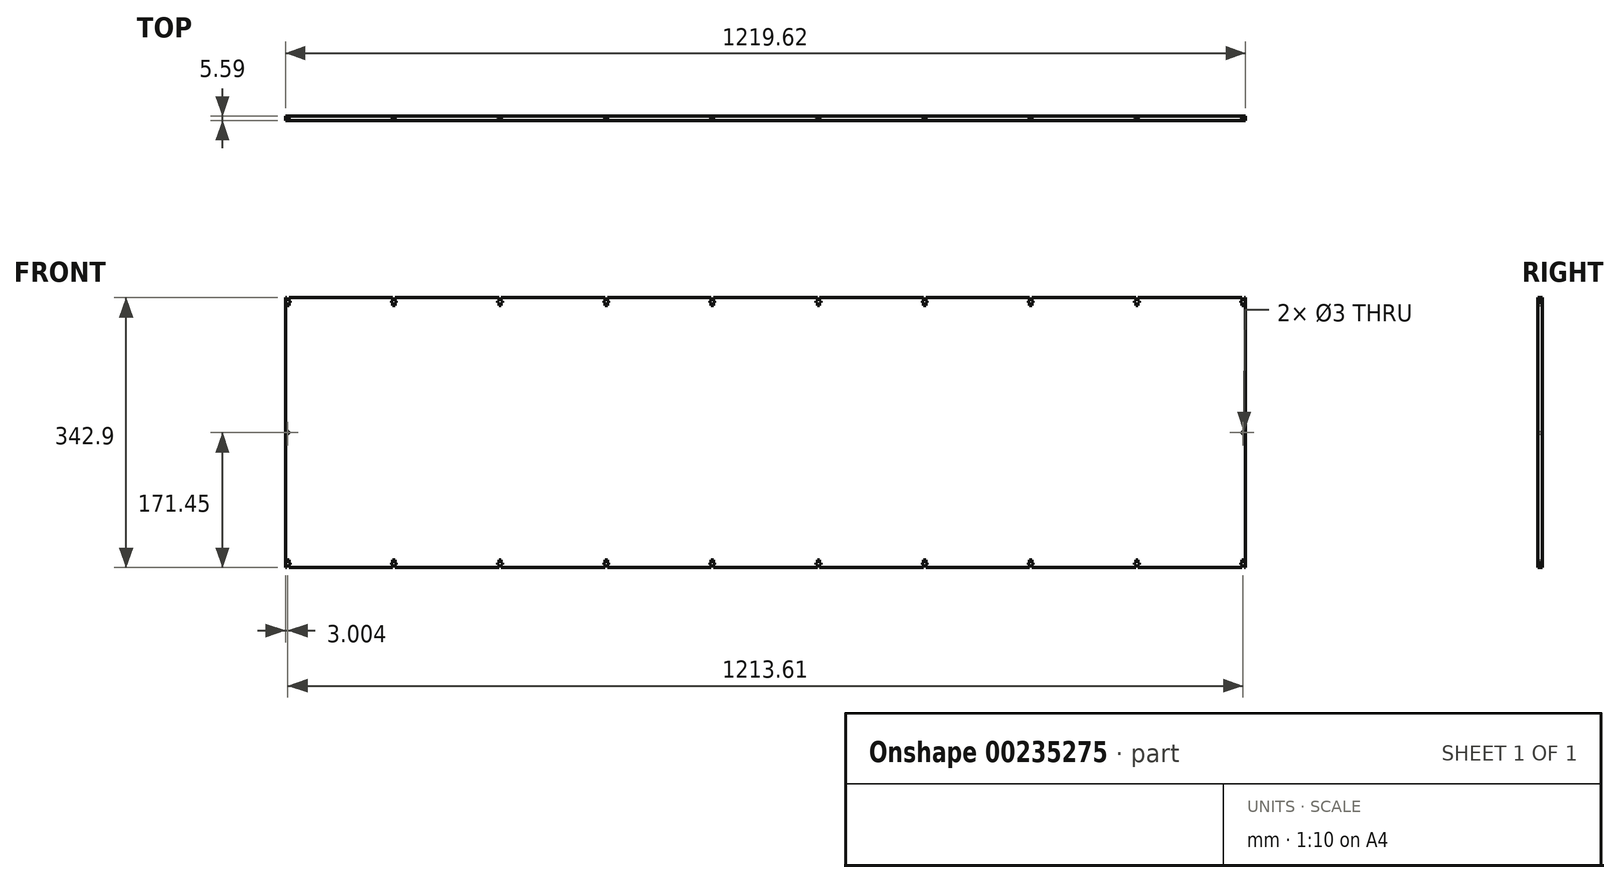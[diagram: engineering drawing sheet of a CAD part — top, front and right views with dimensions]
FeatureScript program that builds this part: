
annotation { "Feature Type Name" : "Feature", "Feature Type Description" : "" }
export const myFeature = defineFeature(function(context is Context, id is Id, definition is map)
    precondition{}
    {
        {
            var Q0;
            Q0=qCreatedBy(makeId("Front.planeOp"),FACE);
            var sketch = newSketch(context, id + "F0", { "sketchPlane" : qUnion([Q0])});
            skLineSegment(sketch, "E0.bottom", {"start": v(-609.6, 171.45) * mm, "end": v(-608.3, 171.45) * mm});
            skLineSegment(sketch, "E0.top", {"start": v(-609.6, -171.45) * mm, "end": v(-608.3, -171.45) * mm});
            skLineSegment(sketch, "E0.left", {"start": v(-609.6, 171.45) * mm, "end": v(-609.6, -171.45) * mm});
            skLineSegment(sketch, "E0.right", {"start": v(609.6, 171.45) * mm, "end": v(609.6, -171.45) * mm});
            skPoint(sketch, "E0.middle", {"position": v(0, 0) * mm});
            skLineSegment(sketch, "E1", {"start": v(-609.6, 171.45) * mm, "end": v(-608.3, 171.45) * mm, "construction": true});
            skLineSegment(sketch, "E2", {"start": v(-606.8, 171.45) * mm, "end": v(-606.8, 139.65) * mm, "construction": true});
            skLineSegment(sketch, "E3", {"start": v(-608.3, 171.45) * mm, "end": v(-608.3, 167.45) * mm});
            skLineSegment(sketch, "E4", {"start": v(-608.3, 167.45) * mm, "end": v(-609.8, 167.45) * mm});
            skLineSegment(sketch, "E5", {"start": v(-609.8, 167.45) * mm, "end": v(-609.8, 165.45) * mm});
            skLineSegment(sketch, "E6", {"start": v(-609.8, 165.45) * mm, "end": v(-608.3, 165.45) * mm});
            skLineSegment(sketch, "E7", {"start": v(-608.3, 165.45) * mm, "end": v(-608.3, 161.45) * mm});
            skLineSegment(sketch, "E8", {"start": v(-608.3, 161.45) * mm, "end": v(-605.3, 161.45) * mm});
            skLineSegment(sketch, "E9", {"start": v(-605.3, 161.45) * mm, "end": v(-605.3, 165.45) * mm});
            skLineSegment(sketch, "E10", {"start": v(-605.3, 165.45) * mm, "end": v(-603.8, 165.45) * mm});
            skLineSegment(sketch, "E11", {"start": v(-603.8, 165.45) * mm, "end": v(-603.8, 167.45) * mm});
            skLineSegment(sketch, "E12", {"start": v(-603.8, 167.45) * mm, "end": v(-605.3, 167.45) * mm});
            skLineSegment(sketch, "E13", {"start": v(-605.3, 167.45) * mm, "end": v(-605.3, 171.45) * mm});
            skLineSegment(sketch, "E14.trimOffspring", {"start": v(-605.3, 171.45) * mm, "end": v(-473.46, 171.45) * mm});
            skLineSegment(sketch, "E15.1.0.0", {"start": v(-470.46, 167.45) * mm, "end": v(-470.46, 171.45) * mm});
            skLineSegment(sketch, "E15.1.0.1", {"start": v(-470.46, 161.45) * mm, "end": v(-470.46, 165.45) * mm});
            skLineSegment(sketch, "E15.1.0.2", {"start": v(-470.46, 165.45) * mm, "end": v(-468.96, 165.45) * mm});
            skLineSegment(sketch, "E15.1.0.3", {"start": v(-468.96, 165.45) * mm, "end": v(-468.96, 167.45) * mm});
            skLineSegment(sketch, "E15.1.0.4", {"start": v(-471.96, 171.45) * mm, "end": v(-471.96, 139.65) * mm, "construction": true});
            skLineSegment(sketch, "E15.1.0.5", {"start": v(-473.46, 171.45) * mm, "end": v(-473.46, 167.45) * mm});
            skLineSegment(sketch, "E15.1.0.6", {"start": v(-473.46, 167.45) * mm, "end": v(-474.96, 167.45) * mm});
            skLineSegment(sketch, "E15.1.0.7", {"start": v(-474.96, 167.45) * mm, "end": v(-474.96, 165.45) * mm});
            skLineSegment(sketch, "E15.1.0.8", {"start": v(-474.96, 165.45) * mm, "end": v(-473.46, 165.45) * mm});
            skLineSegment(sketch, "E15.1.0.9", {"start": v(-473.46, 165.45) * mm, "end": v(-473.46, 161.45) * mm});
            skLineSegment(sketch, "E15.1.0.10", {"start": v(-473.46, 161.45) * mm, "end": v(-470.46, 161.45) * mm});
            skLineSegment(sketch, "E15.1.0.11", {"start": v(-468.96, 167.45) * mm, "end": v(-470.46, 167.45) * mm});
            skLineSegment(sketch, "E15.2.0.0", {"start": v(-335.61, 167.45) * mm, "end": v(-335.61, 171.45) * mm});
            skLineSegment(sketch, "E15.2.0.1", {"start": v(-335.61, 161.45) * mm, "end": v(-335.61, 165.45) * mm});
            skLineSegment(sketch, "E15.2.0.2", {"start": v(-335.61, 165.45) * mm, "end": v(-334.11, 165.45) * mm});
            skLineSegment(sketch, "E15.2.0.3", {"start": v(-334.11, 165.45) * mm, "end": v(-334.11, 167.45) * mm});
            skLineSegment(sketch, "E15.2.0.4", {"start": v(-337.11, 171.45) * mm, "end": v(-337.11, 139.65) * mm, "construction": true});
            skLineSegment(sketch, "E15.2.0.5", {"start": v(-338.61, 171.45) * mm, "end": v(-338.61, 167.45) * mm});
            skLineSegment(sketch, "E15.2.0.6", {"start": v(-338.61, 167.45) * mm, "end": v(-340.11, 167.45) * mm});
            skLineSegment(sketch, "E15.2.0.7", {"start": v(-340.11, 167.45) * mm, "end": v(-340.11, 165.45) * mm});
            skLineSegment(sketch, "E15.2.0.8", {"start": v(-340.11, 165.45) * mm, "end": v(-338.61, 165.45) * mm});
            skLineSegment(sketch, "E15.2.0.9", {"start": v(-338.61, 165.45) * mm, "end": v(-338.61, 161.45) * mm});
            skLineSegment(sketch, "E15.2.0.10", {"start": v(-338.61, 161.45) * mm, "end": v(-335.61, 161.45) * mm});
            skLineSegment(sketch, "E15.2.0.11", {"start": v(-334.11, 167.45) * mm, "end": v(-335.61, 167.45) * mm});
            skLineSegment(sketch, "E15.3.0.0", {"start": v(-200.77, 167.45) * mm, "end": v(-200.77, 171.45) * mm});
            skLineSegment(sketch, "E15.3.0.1", {"start": v(-200.77, 161.45) * mm, "end": v(-200.77, 165.45) * mm});
            skLineSegment(sketch, "E15.3.0.2", {"start": v(-200.77, 165.45) * mm, "end": v(-199.27, 165.45) * mm});
            skLineSegment(sketch, "E15.3.0.3", {"start": v(-199.27, 165.45) * mm, "end": v(-199.27, 167.45) * mm});
            skLineSegment(sketch, "E15.3.0.4", {"start": v(-202.27, 171.45) * mm, "end": v(-202.27, 139.65) * mm, "construction": true});
            skLineSegment(sketch, "E15.3.0.5", {"start": v(-203.77, 171.45) * mm, "end": v(-203.77, 167.45) * mm});
            skLineSegment(sketch, "E15.3.0.6", {"start": v(-203.77, 167.45) * mm, "end": v(-205.27, 167.45) * mm});
            skLineSegment(sketch, "E15.3.0.7", {"start": v(-205.27, 167.45) * mm, "end": v(-205.27, 165.45) * mm});
            skLineSegment(sketch, "E15.3.0.8", {"start": v(-205.27, 165.45) * mm, "end": v(-203.77, 165.45) * mm});
            skLineSegment(sketch, "E15.3.0.9", {"start": v(-203.77, 165.45) * mm, "end": v(-203.77, 161.45) * mm});
            skLineSegment(sketch, "E15.3.0.10", {"start": v(-203.77, 161.45) * mm, "end": v(-200.77, 161.45) * mm});
            skLineSegment(sketch, "E15.3.0.11", {"start": v(-199.27, 167.45) * mm, "end": v(-200.77, 167.45) * mm});
            skLineSegment(sketch, "E15.4.0.0", {"start": v(-65.92, 167.45) * mm, "end": v(-65.92, 171.45) * mm});
            skLineSegment(sketch, "E15.4.0.1", {"start": v(-65.92, 161.45) * mm, "end": v(-65.92, 165.45) * mm});
            skLineSegment(sketch, "E15.4.0.2", {"start": v(-65.92, 165.45) * mm, "end": v(-64.42, 165.45) * mm});
            skLineSegment(sketch, "E15.4.0.3", {"start": v(-64.42, 165.45) * mm, "end": v(-64.42, 167.45) * mm});
            skLineSegment(sketch, "E15.4.0.4", {"start": v(-67.42, 171.45) * mm, "end": v(-67.42, 139.65) * mm, "construction": true});
            skLineSegment(sketch, "E15.4.0.5", {"start": v(-68.92, 171.45) * mm, "end": v(-68.92, 167.45) * mm});
            skLineSegment(sketch, "E15.4.0.6", {"start": v(-68.92, 167.45) * mm, "end": v(-70.42, 167.45) * mm});
            skLineSegment(sketch, "E15.4.0.7", {"start": v(-70.42, 167.45) * mm, "end": v(-70.42, 165.45) * mm});
            skLineSegment(sketch, "E15.4.0.8", {"start": v(-70.42, 165.45) * mm, "end": v(-68.92, 165.45) * mm});
            skLineSegment(sketch, "E15.4.0.9", {"start": v(-68.92, 165.45) * mm, "end": v(-68.92, 161.45) * mm});
            skLineSegment(sketch, "E15.4.0.10", {"start": v(-68.92, 161.45) * mm, "end": v(-65.92, 161.45) * mm});
            skLineSegment(sketch, "E15.4.0.11", {"start": v(-64.42, 167.45) * mm, "end": v(-65.92, 167.45) * mm});
            skLineSegment(sketch, "E15.5.0.0", {"start": v(68.92, 167.45) * mm, "end": v(68.92, 171.45) * mm});
            skLineSegment(sketch, "E15.5.0.1", {"start": v(68.92, 161.45) * mm, "end": v(68.92, 165.45) * mm});
            skLineSegment(sketch, "E15.5.0.2", {"start": v(68.92, 165.45) * mm, "end": v(70.42, 165.45) * mm});
            skLineSegment(sketch, "E15.5.0.3", {"start": v(70.42, 165.45) * mm, "end": v(70.42, 167.45) * mm});
            skLineSegment(sketch, "E15.5.0.4", {"start": v(67.42, 171.45) * mm, "end": v(67.42, 139.65) * mm, "construction": true});
            skLineSegment(sketch, "E15.5.0.5", {"start": v(65.92, 171.45) * mm, "end": v(65.92, 167.45) * mm});
            skLineSegment(sketch, "E15.5.0.6", {"start": v(65.92, 167.45) * mm, "end": v(64.42, 167.45) * mm});
            skLineSegment(sketch, "E15.5.0.7", {"start": v(64.42, 167.45) * mm, "end": v(64.42, 165.45) * mm});
            skLineSegment(sketch, "E15.5.0.8", {"start": v(64.42, 165.45) * mm, "end": v(65.92, 165.45) * mm});
            skLineSegment(sketch, "E15.5.0.9", {"start": v(65.92, 165.45) * mm, "end": v(65.92, 161.45) * mm});
            skLineSegment(sketch, "E15.5.0.10", {"start": v(65.92, 161.45) * mm, "end": v(68.92, 161.45) * mm});
            skLineSegment(sketch, "E15.5.0.11", {"start": v(70.42, 167.45) * mm, "end": v(68.92, 167.45) * mm});
            skLineSegment(sketch, "E15.6.0.0", {"start": v(203.77, 167.45) * mm, "end": v(203.77, 171.45) * mm});
            skLineSegment(sketch, "E15.6.0.1", {"start": v(203.77, 161.45) * mm, "end": v(203.77, 165.45) * mm});
            skLineSegment(sketch, "E15.6.0.2", {"start": v(203.77, 165.45) * mm, "end": v(205.27, 165.45) * mm});
            skLineSegment(sketch, "E15.6.0.3", {"start": v(205.27, 165.45) * mm, "end": v(205.27, 167.45) * mm});
            skLineSegment(sketch, "E15.6.0.4", {"start": v(202.27, 171.45) * mm, "end": v(202.27, 139.65) * mm, "construction": true});
            skLineSegment(sketch, "E15.6.0.5", {"start": v(200.77, 171.45) * mm, "end": v(200.77, 167.45) * mm});
            skLineSegment(sketch, "E15.6.0.6", {"start": v(200.77, 167.45) * mm, "end": v(199.27, 167.45) * mm});
            skLineSegment(sketch, "E15.6.0.7", {"start": v(199.27, 167.45) * mm, "end": v(199.27, 165.45) * mm});
            skLineSegment(sketch, "E15.6.0.8", {"start": v(199.27, 165.45) * mm, "end": v(200.77, 165.45) * mm});
            skLineSegment(sketch, "E15.6.0.9", {"start": v(200.77, 165.45) * mm, "end": v(200.77, 161.45) * mm});
            skLineSegment(sketch, "E15.6.0.10", {"start": v(200.77, 161.45) * mm, "end": v(203.77, 161.45) * mm});
            skLineSegment(sketch, "E15.6.0.11", {"start": v(205.27, 167.45) * mm, "end": v(203.77, 167.45) * mm});
            skLineSegment(sketch, "E15.7.0.0", {"start": v(338.62, 167.45) * mm, "end": v(338.62, 171.45) * mm});
            skLineSegment(sketch, "E15.7.0.1", {"start": v(338.62, 161.45) * mm, "end": v(338.62, 165.45) * mm});
            skLineSegment(sketch, "E15.7.0.2", {"start": v(338.62, 165.45) * mm, "end": v(340.12, 165.45) * mm});
            skLineSegment(sketch, "E15.7.0.3", {"start": v(340.12, 165.45) * mm, "end": v(340.12, 167.45) * mm});
            skLineSegment(sketch, "E15.7.0.4", {"start": v(337.12, 171.45) * mm, "end": v(337.12, 139.65) * mm, "construction": true});
            skLineSegment(sketch, "E15.7.0.5", {"start": v(335.62, 171.45) * mm, "end": v(335.62, 167.45) * mm});
            skLineSegment(sketch, "E15.7.0.6", {"start": v(335.62, 167.45) * mm, "end": v(334.12, 167.45) * mm});
            skLineSegment(sketch, "E15.7.0.7", {"start": v(334.12, 167.45) * mm, "end": v(334.12, 165.45) * mm});
            skLineSegment(sketch, "E15.7.0.8", {"start": v(334.12, 165.45) * mm, "end": v(335.62, 165.45) * mm});
            skLineSegment(sketch, "E15.7.0.9", {"start": v(335.62, 165.45) * mm, "end": v(335.62, 161.45) * mm});
            skLineSegment(sketch, "E15.7.0.10", {"start": v(335.62, 161.45) * mm, "end": v(338.62, 161.45) * mm});
            skLineSegment(sketch, "E15.7.0.11", {"start": v(340.12, 167.45) * mm, "end": v(338.62, 167.45) * mm});
            skLineSegment(sketch, "E15.8.0.0", {"start": v(473.46, 167.45) * mm, "end": v(473.46, 171.45) * mm});
            skLineSegment(sketch, "E15.8.0.1", {"start": v(473.46, 161.45) * mm, "end": v(473.46, 165.45) * mm});
            skLineSegment(sketch, "E15.8.0.2", {"start": v(473.46, 165.45) * mm, "end": v(474.96, 165.45) * mm});
            skLineSegment(sketch, "E15.8.0.3", {"start": v(474.96, 165.45) * mm, "end": v(474.96, 167.45) * mm});
            skLineSegment(sketch, "E15.8.0.4", {"start": v(471.96, 171.45) * mm, "end": v(471.96, 139.65) * mm, "construction": true});
            skLineSegment(sketch, "E15.8.0.5", {"start": v(470.46, 171.45) * mm, "end": v(470.46, 167.45) * mm});
            skLineSegment(sketch, "E15.8.0.6", {"start": v(470.46, 167.45) * mm, "end": v(468.96, 167.45) * mm});
            skLineSegment(sketch, "E15.8.0.7", {"start": v(468.96, 167.45) * mm, "end": v(468.96, 165.45) * mm});
            skLineSegment(sketch, "E15.8.0.8", {"start": v(468.96, 165.45) * mm, "end": v(470.46, 165.45) * mm});
            skLineSegment(sketch, "E15.8.0.9", {"start": v(470.46, 165.45) * mm, "end": v(470.46, 161.45) * mm});
            skLineSegment(sketch, "E15.8.0.10", {"start": v(470.46, 161.45) * mm, "end": v(473.46, 161.45) * mm});
            skLineSegment(sketch, "E15.8.0.11", {"start": v(474.96, 167.45) * mm, "end": v(473.46, 167.45) * mm});
            skLineSegment(sketch, "E15.9.0.0", {"start": v(608.3, 167.45) * mm, "end": v(608.3, 171.45) * mm});
            skLineSegment(sketch, "E15.9.0.1", {"start": v(608.3, 161.45) * mm, "end": v(608.3, 165.45) * mm});
            skLineSegment(sketch, "E15.9.0.2", {"start": v(608.3, 165.45) * mm, "end": v(609.8, 165.45) * mm});
            skLineSegment(sketch, "E15.9.0.3", {"start": v(609.8, 165.45) * mm, "end": v(609.8, 167.45) * mm});
            skLineSegment(sketch, "E15.9.0.4", {"start": v(606.8, 171.45) * mm, "end": v(606.8, 139.65) * mm, "construction": true});
            skLineSegment(sketch, "E15.9.0.5", {"start": v(605.3, 171.45) * mm, "end": v(605.3, 167.45) * mm});
            skLineSegment(sketch, "E15.9.0.6", {"start": v(605.3, 167.45) * mm, "end": v(603.8, 167.45) * mm});
            skLineSegment(sketch, "E15.9.0.7", {"start": v(603.8, 167.45) * mm, "end": v(603.8, 165.45) * mm});
            skLineSegment(sketch, "E15.9.0.8", {"start": v(603.8, 165.45) * mm, "end": v(605.3, 165.45) * mm});
            skLineSegment(sketch, "E15.9.0.9", {"start": v(605.3, 165.45) * mm, "end": v(605.3, 161.45) * mm});
            skLineSegment(sketch, "E15.9.0.10", {"start": v(605.3, 161.45) * mm, "end": v(608.3, 161.45) * mm});
            skLineSegment(sketch, "E15.9.0.11", {"start": v(609.8, 167.45) * mm, "end": v(608.3, 167.45) * mm});
            skLineSegment(sketch, "E15.direction1", {"start": v(-606.8, 139.65) * mm, "end": v(-471.96, 139.65) * mm, "construction": true});
            skLineSegment(sketch, "E16.trimOffspring", {"start": v(608.3, 171.45) * mm, "end": v(609.6, 171.45) * mm});
            skLineSegment(sketch, "E17.trimOffspring", {"start": v(473.46, 171.45) * mm, "end": v(605.3, 171.45) * mm});
            skLineSegment(sketch, "E18.trimOffspring", {"start": v(338.62, 171.45) * mm, "end": v(470.46, 171.45) * mm});
            skLineSegment(sketch, "E19.trimOffspring", {"start": v(203.77, 171.45) * mm, "end": v(335.62, 171.45) * mm});
            skLineSegment(sketch, "E20.trimOffspring", {"start": v(68.92, 171.45) * mm, "end": v(200.77, 171.45) * mm});
            skLineSegment(sketch, "E21.trimOffspring", {"start": v(-65.92, 171.45) * mm, "end": v(65.92, 171.45) * mm});
            skLineSegment(sketch, "E22.trimOffspring", {"start": v(-200.77, 171.45) * mm, "end": v(-68.92, 171.45) * mm});
            skLineSegment(sketch, "E23.trimOffspring", {"start": v(-335.61, 171.45) * mm, "end": v(-203.77, 171.45) * mm});
            skLineSegment(sketch, "E24.trimOffspring", {"start": v(-470.46, 171.45) * mm, "end": v(-338.61, 171.45) * mm});
            skLineSegment(sketch, "E25", {"start": v(0, 0) * mm, "end": v(-483.43, 0) * mm, "construction": true});
            skLineSegment(sketch, "E26.MirrorCS", {"start": v(-603.8, -167.45) * mm, "end": v(-605.3, -167.45) * mm});
            skLineSegment(sketch, "E27.MirrorCS", {"start": v(-605.3, -161.45) * mm, "end": v(-605.3, -165.45) * mm});
            skLineSegment(sketch, "E28.MirrorCS", {"start": v(-605.3, -165.45) * mm, "end": v(-603.8, -165.45) * mm});
            skLineSegment(sketch, "E29.MirrorCS", {"start": v(-603.8, -165.45) * mm, "end": v(-603.8, -167.45) * mm});
            skLineSegment(sketch, "E30.MirrorCS", {"start": v(-606.8, -171.45) * mm, "end": v(-606.8, -139.65) * mm, "construction": true});
            skLineSegment(sketch, "E31.MirrorCS", {"start": v(-608.3, -171.45) * mm, "end": v(-608.3, -167.45) * mm});
            skLineSegment(sketch, "E32.MirrorCS", {"start": v(-608.3, -167.45) * mm, "end": v(-609.8, -167.45) * mm});
            skLineSegment(sketch, "E33.MirrorCS", {"start": v(-605.3, -167.45) * mm, "end": v(-605.3, -171.45) * mm});
            skLineSegment(sketch, "E34.MirrorCS", {"start": v(-608.3, -165.45) * mm, "end": v(-608.3, -161.45) * mm});
            skLineSegment(sketch, "E35.MirrorCS", {"start": v(-608.3, -161.45) * mm, "end": v(-605.3, -161.45) * mm});
            skLineSegment(sketch, "E36.MirrorCS", {"start": v(-609.8, -165.45) * mm, "end": v(-608.3, -165.45) * mm});
            skLineSegment(sketch, "E37.MirrorCS", {"start": v(-609.8, -167.45) * mm, "end": v(-609.8, -165.45) * mm});
            skLineSegment(sketch, "E38.MirrorCS", {"start": v(-470.46, -165.45) * mm, "end": v(-468.96, -165.45) * mm});
            skLineSegment(sketch, "E39.MirrorCS", {"start": v(-468.96, -165.45) * mm, "end": v(-468.96, -167.45) * mm});
            skLineSegment(sketch, "E40.MirrorCS", {"start": v(-473.46, -167.45) * mm, "end": v(-474.96, -167.45) * mm});
            skLineSegment(sketch, "E41.MirrorCS", {"start": v(-474.96, -167.45) * mm, "end": v(-474.96, -165.45) * mm});
            skLineSegment(sketch, "E42.MirrorCS", {"start": v(-474.96, -165.45) * mm, "end": v(-473.46, -165.45) * mm});
            skLineSegment(sketch, "E43.MirrorCS", {"start": v(-468.96, -167.45) * mm, "end": v(-470.46, -167.45) * mm});
            skLineSegment(sketch, "E44.MirrorCS", {"start": v(-470.46, -167.45) * mm, "end": v(-470.46, -171.45) * mm});
            skLineSegment(sketch, "E45.MirrorCS", {"start": v(-470.46, -161.45) * mm, "end": v(-470.46, -165.45) * mm});
            skLineSegment(sketch, "E46.MirrorCS", {"start": v(-471.96, -171.45) * mm, "end": v(-471.96, -139.65) * mm, "construction": true});
            skLineSegment(sketch, "E47.MirrorCS", {"start": v(-473.46, -171.45) * mm, "end": v(-473.46, -167.45) * mm});
            skLineSegment(sketch, "E48.MirrorCS", {"start": v(-473.46, -161.45) * mm, "end": v(-470.46, -161.45) * mm});
            skLineSegment(sketch, "E49.MirrorCS", {"start": v(-473.46, -165.45) * mm, "end": v(-473.46, -161.45) * mm});
            skLineSegment(sketch, "E50.MirrorCS", {"start": v(-334.11, -165.45) * mm, "end": v(-334.11, -167.45) * mm});
            skLineSegment(sketch, "E51.MirrorCS", {"start": v(-335.61, -165.45) * mm, "end": v(-334.11, -165.45) * mm});
            skLineSegment(sketch, "E52.MirrorCS", {"start": v(-334.11, -167.45) * mm, "end": v(-335.61, -167.45) * mm});
            skLineSegment(sketch, "E53.MirrorCS", {"start": v(-340.11, -165.45) * mm, "end": v(-338.61, -165.45) * mm});
            skLineSegment(sketch, "E54.MirrorCS", {"start": v(-340.11, -167.45) * mm, "end": v(-340.11, -165.45) * mm});
            skLineSegment(sketch, "E55.MirrorCS", {"start": v(-338.61, -167.45) * mm, "end": v(-340.11, -167.45) * mm});
            skLineSegment(sketch, "E56.MirrorCS", {"start": v(-335.61, -161.45) * mm, "end": v(-335.61, -165.45) * mm});
            skLineSegment(sketch, "E57.MirrorCS", {"start": v(-337.11, -171.45) * mm, "end": v(-337.11, -139.65) * mm, "construction": true});
            skLineSegment(sketch, "E58.MirrorCS", {"start": v(-335.61, -167.45) * mm, "end": v(-335.61, -171.45) * mm});
            skLineSegment(sketch, "E59.MirrorCS", {"start": v(-338.61, -161.45) * mm, "end": v(-335.61, -161.45) * mm});
            skLineSegment(sketch, "E60.MirrorCS", {"start": v(-338.61, -165.45) * mm, "end": v(-338.61, -161.45) * mm});
            skLineSegment(sketch, "E61.MirrorCS", {"start": v(-338.61, -171.45) * mm, "end": v(-338.61, -167.45) * mm});
            skLineSegment(sketch, "E62.MirrorCS", {"start": v(-205.27, -167.45) * mm, "end": v(-205.27, -165.45) * mm});
            skLineSegment(sketch, "E63.MirrorCS", {"start": v(-203.77, -167.45) * mm, "end": v(-205.27, -167.45) * mm});
            skLineSegment(sketch, "E64.MirrorCS", {"start": v(-205.27, -165.45) * mm, "end": v(-203.77, -165.45) * mm});
            skLineSegment(sketch, "E65.MirrorCS", {"start": v(-199.27, -167.45) * mm, "end": v(-200.77, -167.45) * mm});
            skLineSegment(sketch, "E66.MirrorCS", {"start": v(-200.77, -165.45) * mm, "end": v(-199.27, -165.45) * mm});
            skLineSegment(sketch, "E67.MirrorCS", {"start": v(-199.27, -165.45) * mm, "end": v(-199.27, -167.45) * mm});
            skLineSegment(sketch, "E68.MirrorCS", {"start": v(-203.77, -165.45) * mm, "end": v(-203.77, -161.45) * mm});
            skLineSegment(sketch, "E69.MirrorCS", {"start": v(-203.77, -161.45) * mm, "end": v(-200.77, -161.45) * mm});
            skLineSegment(sketch, "E70.MirrorCS", {"start": v(-200.77, -167.45) * mm, "end": v(-200.77, -171.45) * mm});
            skLineSegment(sketch, "E71.MirrorCS", {"start": v(-200.77, -161.45) * mm, "end": v(-200.77, -165.45) * mm});
            skLineSegment(sketch, "E72.MirrorCS", {"start": v(-202.27, -171.45) * mm, "end": v(-202.27, -139.65) * mm, "construction": true});
            skLineSegment(sketch, "E73.MirrorCS", {"start": v(-203.77, -171.45) * mm, "end": v(-203.77, -167.45) * mm});
            skLineSegment(sketch, "E74.MirrorCS", {"start": v(-64.42, -167.45) * mm, "end": v(-65.92, -167.45) * mm});
            skLineSegment(sketch, "E75.MirrorCS", {"start": v(-70.42, -165.45) * mm, "end": v(-68.92, -165.45) * mm});
            skLineSegment(sketch, "E76.MirrorCS", {"start": v(-70.42, -167.45) * mm, "end": v(-70.42, -165.45) * mm});
            skLineSegment(sketch, "E77.MirrorCS", {"start": v(-68.92, -167.45) * mm, "end": v(-70.42, -167.45) * mm});
            skLineSegment(sketch, "E78.MirrorCS", {"start": v(-64.42, -165.45) * mm, "end": v(-64.42, -167.45) * mm});
            skLineSegment(sketch, "E79.MirrorCS", {"start": v(-65.92, -165.45) * mm, "end": v(-64.42, -165.45) * mm});
            skLineSegment(sketch, "E80.MirrorCS", {"start": v(-68.92, -161.45) * mm, "end": v(-65.92, -161.45) * mm});
            skLineSegment(sketch, "E81.MirrorCS", {"start": v(-68.92, -165.45) * mm, "end": v(-68.92, -161.45) * mm});
            skLineSegment(sketch, "E82.MirrorCS", {"start": v(-68.92, -171.45) * mm, "end": v(-68.92, -167.45) * mm});
            skLineSegment(sketch, "E83.MirrorCS", {"start": v(-67.42, -171.45) * mm, "end": v(-67.42, -139.65) * mm, "construction": true});
            skLineSegment(sketch, "E84.MirrorCS", {"start": v(-65.92, -161.45) * mm, "end": v(-65.92, -165.45) * mm});
            skLineSegment(sketch, "E85.MirrorCS", {"start": v(-65.92, -167.45) * mm, "end": v(-65.92, -171.45) * mm});
            skLineSegment(sketch, "E86.MirrorCS", {"start": v(68.92, -165.45) * mm, "end": v(70.42, -165.45) * mm});
            skLineSegment(sketch, "E87.MirrorCS", {"start": v(70.42, -165.45) * mm, "end": v(70.42, -167.45) * mm});
            skLineSegment(sketch, "E88.MirrorCS", {"start": v(65.92, -167.45) * mm, "end": v(64.42, -167.45) * mm});
            skLineSegment(sketch, "E89.MirrorCS", {"start": v(64.42, -167.45) * mm, "end": v(64.42, -165.45) * mm});
            skLineSegment(sketch, "E90.MirrorCS", {"start": v(64.42, -165.45) * mm, "end": v(65.92, -165.45) * mm});
            skLineSegment(sketch, "E91.MirrorCS", {"start": v(70.42, -167.45) * mm, "end": v(68.92, -167.45) * mm});
            skLineSegment(sketch, "E92.MirrorCS", {"start": v(68.92, -167.45) * mm, "end": v(68.92, -171.45) * mm});
            skLineSegment(sketch, "E93.MirrorCS", {"start": v(68.92, -161.45) * mm, "end": v(68.92, -165.45) * mm});
            skLineSegment(sketch, "E94.MirrorCS", {"start": v(67.42, -171.45) * mm, "end": v(67.42, -139.65) * mm, "construction": true});
            skLineSegment(sketch, "E95.MirrorCS", {"start": v(65.92, -171.45) * mm, "end": v(65.92, -167.45) * mm});
            skLineSegment(sketch, "E96.MirrorCS", {"start": v(65.92, -161.45) * mm, "end": v(68.92, -161.45) * mm});
            skLineSegment(sketch, "E97.MirrorCS", {"start": v(65.92, -165.45) * mm, "end": v(65.92, -161.45) * mm});
            skLineSegment(sketch, "E98.MirrorCS", {"start": v(205.27, -165.45) * mm, "end": v(205.27, -167.45) * mm});
            skLineSegment(sketch, "E99.MirrorCS", {"start": v(203.77, -165.45) * mm, "end": v(205.27, -165.45) * mm});
            skLineSegment(sketch, "E100.MirrorCS", {"start": v(200.77, -171.45) * mm, "end": v(200.77, -167.45) * mm});
            skLineSegment(sketch, "E101.MirrorCS", {"start": v(203.77, -167.45) * mm, "end": v(203.77, -171.45) * mm});
            skLineSegment(sketch, "E102.MirrorCS", {"start": v(205.27, -167.45) * mm, "end": v(203.77, -167.45) * mm});
            skLineSegment(sketch, "E103.MirrorCS", {"start": v(199.27, -165.45) * mm, "end": v(200.77, -165.45) * mm});
            skLineSegment(sketch, "E104.MirrorCS", {"start": v(200.77, -167.45) * mm, "end": v(199.27, -167.45) * mm});
            skLineSegment(sketch, "E105.MirrorCS", {"start": v(199.27, -167.45) * mm, "end": v(199.27, -165.45) * mm});
            skLineSegment(sketch, "E106.MirrorCS", {"start": v(202.27, -171.45) * mm, "end": v(202.27, -139.65) * mm, "construction": true});
            skLineSegment(sketch, "E107.MirrorCS", {"start": v(203.77, -161.45) * mm, "end": v(203.77, -165.45) * mm});
            skLineSegment(sketch, "E108.MirrorCS", {"start": v(200.77, -161.45) * mm, "end": v(203.77, -161.45) * mm});
            skLineSegment(sketch, "E109.MirrorCS", {"start": v(200.77, -165.45) * mm, "end": v(200.77, -161.45) * mm});
            skLineSegment(sketch, "E110.MirrorCS", {"start": v(334.12, -167.45) * mm, "end": v(334.12, -165.45) * mm});
            skLineSegment(sketch, "E111.MirrorCS", {"start": v(334.12, -165.45) * mm, "end": v(335.62, -165.45) * mm});
            skLineSegment(sketch, "E112.MirrorCS", {"start": v(335.62, -167.45) * mm, "end": v(334.12, -167.45) * mm});
            skLineSegment(sketch, "E113.MirrorCS", {"start": v(340.12, -167.45) * mm, "end": v(338.62, -167.45) * mm});
            skLineSegment(sketch, "E114.MirrorCS", {"start": v(338.62, -165.45) * mm, "end": v(340.12, -165.45) * mm});
            skLineSegment(sketch, "E115.MirrorCS", {"start": v(340.12, -165.45) * mm, "end": v(340.12, -167.45) * mm});
            skLineSegment(sketch, "E116.MirrorCS", {"start": v(335.62, -165.45) * mm, "end": v(335.62, -161.45) * mm});
            skLineSegment(sketch, "E117.MirrorCS", {"start": v(335.62, -161.45) * mm, "end": v(338.62, -161.45) * mm});
            skLineSegment(sketch, "E118.MirrorCS", {"start": v(335.62, -171.45) * mm, "end": v(335.62, -167.45) * mm});
            skLineSegment(sketch, "E119.MirrorCS", {"start": v(338.62, -167.45) * mm, "end": v(338.62, -171.45) * mm});
            skLineSegment(sketch, "E120.MirrorCS", {"start": v(338.62, -161.45) * mm, "end": v(338.62, -165.45) * mm});
            skLineSegment(sketch, "E121.MirrorCS", {"start": v(337.12, -171.45) * mm, "end": v(337.12, -139.65) * mm, "construction": true});
            skLineSegment(sketch, "E122.MirrorCS", {"start": v(474.96, -167.45) * mm, "end": v(473.46, -167.45) * mm});
            skLineSegment(sketch, "E123.MirrorCS", {"start": v(468.96, -165.45) * mm, "end": v(470.46, -165.45) * mm});
            skLineSegment(sketch, "E124.MirrorCS", {"start": v(468.96, -167.45) * mm, "end": v(468.96, -165.45) * mm});
            skLineSegment(sketch, "E125.MirrorCS", {"start": v(470.46, -167.45) * mm, "end": v(468.96, -167.45) * mm});
            skLineSegment(sketch, "E126.MirrorCS", {"start": v(474.96, -165.45) * mm, "end": v(474.96, -167.45) * mm});
            skLineSegment(sketch, "E127.MirrorCS", {"start": v(473.46, -165.45) * mm, "end": v(474.96, -165.45) * mm});
            skLineSegment(sketch, "E128.MirrorCS", {"start": v(470.46, -161.45) * mm, "end": v(473.46, -161.45) * mm});
            skLineSegment(sketch, "E129.MirrorCS", {"start": v(470.46, -165.45) * mm, "end": v(470.46, -161.45) * mm});
            skLineSegment(sketch, "E130.MirrorCS", {"start": v(470.46, -171.45) * mm, "end": v(470.46, -167.45) * mm});
            skLineSegment(sketch, "E131.MirrorCS", {"start": v(471.96, -171.45) * mm, "end": v(471.96, -139.65) * mm, "construction": true});
            skLineSegment(sketch, "E132.MirrorCS", {"start": v(473.46, -161.45) * mm, "end": v(473.46, -165.45) * mm});
            skLineSegment(sketch, "E133.MirrorCS", {"start": v(473.46, -167.45) * mm, "end": v(473.46, -171.45) * mm});
            skLineSegment(sketch, "E134.MirrorCS", {"start": v(605.3, -167.45) * mm, "end": v(603.8, -167.45) * mm});
            skLineSegment(sketch, "E135.MirrorCS", {"start": v(603.8, -167.45) * mm, "end": v(603.8, -165.45) * mm});
            skLineSegment(sketch, "E136.MirrorCS", {"start": v(603.8, -165.45) * mm, "end": v(605.3, -165.45) * mm});
            skLineSegment(sketch, "E137.MirrorCS", {"start": v(608.3, -161.45) * mm, "end": v(608.3, -165.45) * mm});
            skLineSegment(sketch, "E138.MirrorCS", {"start": v(605.3, -161.45) * mm, "end": v(608.3, -161.45) * mm});
            skLineSegment(sketch, "E139.MirrorCS", {"start": v(605.3, -165.45) * mm, "end": v(605.3, -161.45) * mm});
            skLineSegment(sketch, "E140.MirrorCS", {"start": v(609.8, -165.45) * mm, "end": v(609.8, -167.45) * mm});
            skLineSegment(sketch, "E141.trimOffspring", {"start": v(-605.3, -171.45) * mm, "end": v(-473.46, -171.45) * mm});
            skLineSegment(sketch, "E142.trimOffspring", {"start": v(-470.46, -171.45) * mm, "end": v(-338.61, -171.45) * mm});
            skLineSegment(sketch, "E143.trimOffspring", {"start": v(-335.61, -171.45) * mm, "end": v(-203.77, -171.45) * mm});
            skLineSegment(sketch, "E144.trimOffspring", {"start": v(-200.77, -171.45) * mm, "end": v(-68.92, -171.45) * mm});
            skLineSegment(sketch, "E145.trimOffspring", {"start": v(-65.92, -171.45) * mm, "end": v(65.92, -171.45) * mm});
            skLineSegment(sketch, "E146.trimOffspring", {"start": v(68.92, -171.45) * mm, "end": v(200.77, -171.45) * mm});
            skLineSegment(sketch, "E147.trimOffspring", {"start": v(203.77, -171.45) * mm, "end": v(335.62, -171.45) * mm});
            skLineSegment(sketch, "E148.trimOffspring", {"start": v(338.62, -171.45) * mm, "end": v(470.46, -171.45) * mm});
            skLineSegment(sketch, "E149.trimOffspring", {"start": v(473.46, -171.45) * mm, "end": v(605.3, -171.45) * mm});
            skLineSegment(sketch, "E150", {"start": v(608.3, -165.45) * mm, "end": v(609.8, -165.45) * mm});
            skLineSegment(sketch, "E151", {"start": v(609.8, -167.45) * mm, "end": v(608.3, -167.45) * mm});
            skLineSegment(sketch, "E152", {"start": v(608.3, -167.45) * mm, "end": v(608.3, -171.45) * mm});
            skLineSegment(sketch, "E153", {"start": v(605.3, -167.45) * mm, "end": v(605.3, -171.45) * mm});
            skLineSegment(sketch, "E154.trimOffspring", {"start": v(608.3, -171.45) * mm, "end": v(609.6, -171.45) * mm});
            skLineSegment(sketch, "E155", {"start": v(-609.6, 0) * mm, "end": v(-606.8, 0) * mm, "construction": true});
            skCircle(sketch, "E156", {"center": v(-606.8, 0) * mm, "radius": 1.5 * mm});
            skLineSegment(sketch, "E157", {"start": v(609.6, 0) * mm, "end": v(606.8, 0) * mm});
            skCircle(sketch, "E158", {"center": v(606.8, 0) * mm, "radius": 1.5 * mm});
            skSolve(sketch);
        }
        {
            var Q0;
            Q0 = qSketchRegion(id + "F0", true);
            extrude(context, id + "F1", {"entities" : qUnion([Q0]), "depth" : 5.6 * mm});
        }
    });
